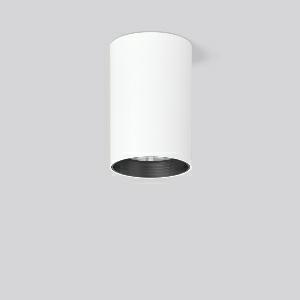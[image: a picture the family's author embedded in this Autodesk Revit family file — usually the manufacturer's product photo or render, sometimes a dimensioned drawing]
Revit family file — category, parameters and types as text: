
# Revit family: heledon_maxi_a_931249_002_2_d51f
name_source: partatom
category: Lighting Fixtures
units: mm (PartAtom-declared; Revit-internal decimal feet)

## family parameters
Cut with Voids When Loaded = No
Host = Face
Light Source = No
Part Type = Normal
Room Calculation Point = No
Round Connector Dimension = Use Diameter
Shared = No

## types (1)
- HELEDON maxi A (1 x LED Modul 927 bakery, 2850 lm, 2700)
    Apparent Load = 33 VA
    Approval mark = CE
    CIE Flux Codes = 96 99 100 100 100
    Color Rendering = 90
    Color Temperature = 2700
    Default Elevation = 1800 mm
    Description = Series: HELEDON maxi
Cylindrical surface-mounted downlight. Housing: die-cast aluminium, powder-coated. Internal ceiling frame polycarbonate with bayonet mounting. Black plastic ring and recessed LED to prevent glare from the side. Optical assembly with lens made of plastic (polycarbonate) for the best homogeneous light distribution - can be changed without tools. Special LED for illumination of pastries included. Suitable for Ceiling mounting. Easy installation with a separate ceiling frame with bayonet mounting and plug connection. Driver integrated. Connected via plug-in connector. High quality converter without flickering and stroboscopic effect. The following accessories can be mounted without use of tools: interchangeable lenses, decorative glasses, honeycomb louvre, clear and frosted diffusers, white interchangeable plastic ring. 
Colour: traffic white, matt (RAL 9016)
Diameter: 123 mm
Height: 183 mm
Lamp: LED
Socket: without socket
Colour temperature: bakery
Colour rendering index (CRI): 97
System power: 33 W
Rated luminous flux: 2850 lm
Luminous efficiency: 86 lm/W
Control gear: Regulated power supply
Protection class: I
Type of protection: IP 20
    Height = 183 mm
    Lamp = 1 x LED Modul 927 bakery
    Lamp Light Flux = 2850 lm
    Lamp count = 1
    Length = 123 mm
    Lifetime = 50000 h
    Luminous efficacy = 86 lm/W
    Manufacturer = RZB
    ModVariant = No
    Model = 931249.002.2
    Mounting Place = Ceiling
    Mounting Type = Surface mounted
    Number of Poles = 1
    OnlyDefault = Yes
    Power Factor = 1
    Product Name = HELEDON maxi A
    Product group = Surface mounted downlights
    ProductGroupID = 302
    Protection Class = Protection class I
    Protection Degree = IP 20
    RLX_Detail_Level = 1
    RLX_Emergency_Light_Flux = 0 lm
    RLX_Emergency_Type = 0
    RLX_Emergency_Type_DB = No
    RlxData = <blob elided: 99077 chars, md5=62ce71ff>
    Socket = socket
    Standby Power = 0 W
    System Light Flux = 2850 lm
    System Power = 33 W
    Type Comments = Product without accessories
    Type Image = 931193.002.jpg
    URL = http://relux.com
    VarID = ---
    Voltage = 230 V
    Voltage Range = 220-240 V
    Weight = 0.00 kg
    Width = 0 mm  [stored 0 ft]

note: [stored X ft] marks values corroborated as IEEE doubles in the binary element streams (Revit-internal decimal feet)

## geometry (parser evidence)
native form markers: Blend x4, Sweep x10
no freeform markers — native parametric forms only
